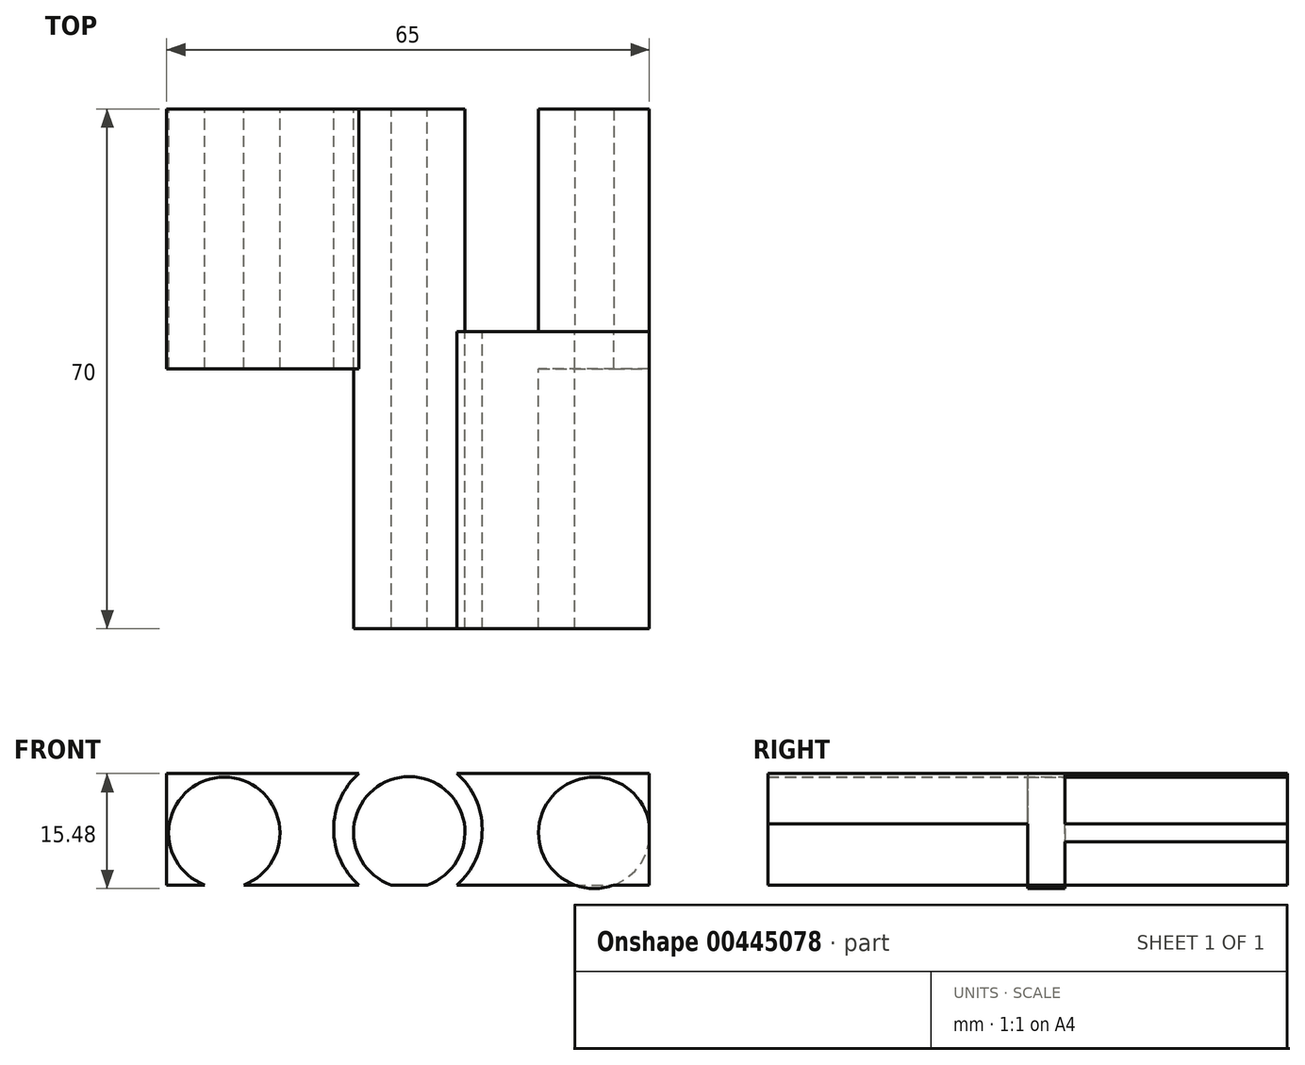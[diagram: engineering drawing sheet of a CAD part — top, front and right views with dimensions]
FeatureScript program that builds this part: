
annotation { "Feature Type Name" : "Feature", "Feature Type Description" : "" }
export const myFeature = defineFeature(function(context is Context, id is Id, definition is map)
    precondition{}
    {
        {
            var Q0;
            Q0=qCreatedBy(makeId("Front.planeOp"),FACE);
            var sketch = newSketch(context, id + "F0", { "sketchPlane" : qUnion([Q0])});
            skLineSegment(sketch, "E0.bottom", {"start": v(-32.5, 7.5) * mm, "end": v(32.5, 7.5) * mm});
            skLineSegment(sketch, "E0.top", {"start": v(-32.5, -7.5) * mm, "end": v(32.5, -7.5) * mm});
            skLineSegment(sketch, "E0.left", {"start": v(-32.5, 7.5) * mm, "end": v(-32.5, -7.5) * mm});
            skLineSegment(sketch, "E0.right", {"start": v(32.5, 7.5) * mm, "end": v(32.5, -7.5) * mm});
            skPoint(sketch, "E0.middle", {"position": v(0, 0) * mm});
            skPoint(sketch, "E1", {"position": v(0.19, -0.4) * mm});
            skCircle(sketch, "E2", {"center": v(0.19, -0.4) * mm, "radius": 7.5 * mm});
            skCircle(sketch, "E3", {"center": v(-24.73, -0.48) * mm, "radius": 7.5 * mm});
            skPoint(sketch, "E3.second.point", {"position": v(-32.23, -0.48) * mm});
            skPoint(sketch, "E3.third.point", {"position": v(-26.42, 6.83) * mm});
            skPoint(sketch, "E4.MirrorP", {"position": v(26.8, 6.83) * mm});
            skCircle(sketch, "E5.MirrorC", {"center": v(25.1, -0.48) * mm, "radius": 7.5 * mm});
            skCircle(sketch, "E6", {"center": v(0, 0) * mm, "radius": 10 * mm});
            skSolve(sketch);
        }
        {
            var Q0;
            {var subQ0=sQuery(id+"F0.wireOp",EDGE,"E3");var subQ1=sQuery(id+"F0.wireOp",EDGE,"E0.top");var subQ2=makeQuery(id+"F0.imprint","INTERSECT",VERTEX,{"disambiguationData":[OD(0.0)],"derivedFrom":[subQ1,subQ0]});Q0=makeQuery(id+"F0.imprint","IMPRINT",FACE,{"disambiguationData":[TD([[makeQuery(id+"F0.imprint","IMPRINT",EDGE,{"disambiguationData":[TD([[subQ2,-1.0]])],"derivedFrom":subQ1}),-1.0]])]});}
            var Q1;
            {var subQ0=sQuery(id+"F0.wireOp",EDGE,"E5.MirrorC");var subQ1=sQuery(id+"F0.wireOp",EDGE,"E0.top");var subQ2=makeQuery(id+"F0.imprint","INTERSECT",VERTEX,{"disambiguationData":[OD(0.0)],"derivedFrom":[subQ1,subQ0]});Q1=makeQuery(id+"F0.imprint","IMPRINT",FACE,{"disambiguationData":[TD([[makeQuery(id+"F0.imprint","IMPRINT",EDGE,{"disambiguationData":[TD([[subQ2,-1.0]])],"derivedFrom":subQ1}),-1.0]])]});}
            var Q2;
            {var subQ0=sQuery(id+"F0.wireOp",EDGE,"E0.right");var subQ1=sQuery(id+"F0.wireOp",EDGE,"E0.top");var subQ2=makeQuery(id+"F0.imprint","INTERSECT",VERTEX,{"derivedFrom":[subQ1,subQ0]});Q2=makeQuery(id+"F0.imprint","IMPRINT",FACE,{"disambiguationData":[TD([[makeQuery(id+"F0.imprint","IMPRINT",EDGE,{"disambiguationData":[TD([[subQ2,1.0]])],"derivedFrom":subQ1}),1.0]])]});}
            var Q3;
            {var subQ0=sQuery(id+"F0.wireOp",EDGE,"E5.MirrorC");var subQ1=sQuery(id+"F0.wireOp",EDGE,"E0.right");var subQ2=makeQuery(id+"F0.imprint","INTERSECT",VERTEX,{"disambiguationData":[OD(0.0)],"derivedFrom":[subQ1,subQ0]});Q3=makeQuery(id+"F0.imprint","IMPRINT",FACE,{"disambiguationData":[TD([[makeQuery(id+"F0.imprint","IMPRINT",EDGE,{"disambiguationData":[TD([[subQ2,-1.0]])],"derivedFrom":subQ1}),1.0]])]});}
            var Q4;
            {var subQ3=sQuery(id+"F0.wireOp",EDGE,"E0.right");var subQ5=sQuery(id+"F0.wireOp",EDGE,"E0.bottom");var subQ6=makeQuery(id+"F0.imprint","INTERSECT",VERTEX,{"derivedFrom":[subQ5,subQ3]});Q4=makeQuery(id+"F0.imprint","IMPRINT",FACE,{"disambiguationData":[TD([[makeQuery(id+"F0.imprint","IMPRINT",EDGE,{"disambiguationData":[TD([[subQ6,1.0]])],"derivedFrom":subQ5}),-1.0]])]});}
            var Q5;
            {var subQ4=sQuery(id+"F0.wireOp",EDGE,"E6");var subQ7=sQuery(id+"F0.wireOp",EDGE,"E0.bottom");var subQ8=makeQuery(id+"F0.imprint","INTERSECT",VERTEX,{"disambiguationData":[OD(0.0)],"derivedFrom":[subQ7,subQ4]});Q5=makeQuery(id+"F0.imprint","IMPRINT",FACE,{"disambiguationData":[TD([[makeQuery(id+"F0.imprint","IMPRINT",EDGE,{"disambiguationData":[TD([[subQ8,-1.0]])],"derivedFrom":subQ7}),-1.0]])]});}
            var Q6;
            {var subQ0=sQuery(id+"F0.wireOp",EDGE,"E0.left");Q6=makeQuery(id+"F0.imprint","IMPRINT",FACE,{"disambiguationData":[TD([[makeQuery(id+"F0.imprint","IMPRINT",EDGE,{"derivedFrom":subQ0}),1.0]])]});}
            var Q7;
            {var subQ0=sQuery(id+"F0.wireOp",EDGE,"E2");var subQ1=sQuery(id+"F0.wireOp",EDGE,"E0.top");var subQ2=makeQuery(id+"F0.imprint","INTERSECT",VERTEX,{"disambiguationData":[OD(0.0)],"derivedFrom":[subQ1,subQ0]});Q7=makeQuery(id+"F0.imprint","IMPRINT",FACE,{"disambiguationData":[TD([[makeQuery(id+"F0.imprint","IMPRINT",EDGE,{"disambiguationData":[TD([[subQ2,-1.0]])],"derivedFrom":subQ1}),1.0]])]});}
            var Q8;
            {var subQ0=sQuery(id+"F0.wireOp",EDGE,"E3");var subQ1=sQuery(id+"F0.wireOp",EDGE,"E0.top");var subQ2=makeQuery(id+"F0.imprint","INTERSECT",VERTEX,{"disambiguationData":[OD(0.0)],"derivedFrom":[subQ1,subQ0]});Q8=makeQuery(id+"F0.imprint","IMPRINT",FACE,{"disambiguationData":[TD([[makeQuery(id+"F0.imprint","IMPRINT",EDGE,{"disambiguationData":[TD([[subQ2,-1.0]])],"derivedFrom":subQ1}),1.0]])]});}
            var Q9;
            {var subQ0=sQuery(id+"F0.wireOp",EDGE,"E5.MirrorC");var subQ1=sQuery(id+"F0.wireOp",EDGE,"E0.top");var subQ2=makeQuery(id+"F0.imprint","INTERSECT",VERTEX,{"disambiguationData":[OD(0.0)],"derivedFrom":[subQ1,subQ0]});Q9=makeQuery(id+"F0.imprint","IMPRINT",FACE,{"disambiguationData":[TD([[makeQuery(id+"F0.imprint","IMPRINT",EDGE,{"disambiguationData":[TD([[subQ2,-1.0]])],"derivedFrom":subQ1}),1.0]])]});}
            extrude(context, id + "F1", {"entities" : qUnion([Q0, Q1, Q2, Q3, Q4, Q5, Q6, Q7, Q8, Q9]), "depth" : 5 * mm});
        }
        {
            var Q0;
            {var subQ0=sQuery(id+"F0.wireOp",EDGE,"E2");var subQ1=sQuery(id+"F0.wireOp",EDGE,"E0.top");var subQ2=makeQuery(id+"F0.imprint","INTERSECT",VERTEX,{"disambiguationData":[OD(0.0)],"derivedFrom":[subQ1,subQ0]});Q0=makeQuery(id+"F0.imprint","IMPRINT",FACE,{"disambiguationData":[TD([[makeQuery(id+"F0.imprint","IMPRINT",EDGE,{"disambiguationData":[TD([[subQ2,-1.0]])],"derivedFrom":subQ1}),1.0]])]});}
            var Q1;
            {var subQ0=sQuery(id+"F0.wireOp",EDGE,"E6");var subQ1=sQuery(id+"F0.wireOp",EDGE,"E0.bottom");var subQ2=makeQuery(id+"F0.imprint","INTERSECT",VERTEX,{"disambiguationData":[OD(0.0)],"derivedFrom":[subQ1,subQ0]});Q1=makeQuery(id+"F0.imprint","IMPRINT",FACE,{"disambiguationData":[TD([[makeQuery(id+"F0.imprint","IMPRINT",EDGE,{"disambiguationData":[TD([[subQ2,-1.0]])],"derivedFrom":subQ1}),1.0]])]});}
            var Q2;
            {var subQ0=sQuery(id+"F0.wireOp",EDGE,"E6");var subQ1=sQuery(id+"F0.wireOp",EDGE,"E0.top");var subQ2=makeQuery(id+"F0.imprint","INTERSECT",VERTEX,{"disambiguationData":[OD(0.0)],"derivedFrom":[subQ1,subQ0]});Q2=makeQuery(id+"F0.imprint","IMPRINT",FACE,{"disambiguationData":[TD([[makeQuery(id+"F0.imprint","IMPRINT",EDGE,{"disambiguationData":[TD([[subQ2,-1.0]])],"derivedFrom":subQ1}),-1.0]])]});}
            var Q3;
            {var subQ4=sQuery(id+"F0.wireOp",EDGE,"E6");var subQ7=sQuery(id+"F0.wireOp",EDGE,"E0.bottom");var subQ8=makeQuery(id+"F0.imprint","INTERSECT",VERTEX,{"disambiguationData":[OD(0.0)],"derivedFrom":[subQ7,subQ4]});Q3=makeQuery(id+"F0.imprint","IMPRINT",FACE,{"disambiguationData":[TD([[makeQuery(id+"F0.imprint","IMPRINT",EDGE,{"disambiguationData":[TD([[subQ8,-1.0]])],"derivedFrom":subQ7}),-1.0]])]});}
            extrude(context, id + "F2", {"entities" : qUnion([Q0, Q1, Q2, Q3]), "operationType" : NewBodyOperationType.ADD, "depth" : 40 * mm});
        }
        {
            var Q0;
            {var subQ0=sQuery(id+"F0.wireOp",EDGE,"E5.MirrorC");var subQ1=sQuery(id+"F0.wireOp",EDGE,"E0.top");var subQ2=makeQuery(id+"F0.imprint","INTERSECT",VERTEX,{"disambiguationData":[OD(0.0)],"derivedFrom":[subQ1,subQ0]});Q0=makeQuery(id+"F0.imprint","IMPRINT",FACE,{"disambiguationData":[TD([[makeQuery(id+"F0.imprint","IMPRINT",EDGE,{"disambiguationData":[TD([[subQ2,-1.0]])],"derivedFrom":subQ1}),1.0]])]});}
            var Q1;
            {var subQ0=sQuery(id+"F0.wireOp",EDGE,"E3");var subQ1=sQuery(id+"F0.wireOp",EDGE,"E0.top");var subQ2=makeQuery(id+"F0.imprint","INTERSECT",VERTEX,{"disambiguationData":[OD(0.0)],"derivedFrom":[subQ1,subQ0]});Q1=makeQuery(id+"F0.imprint","IMPRINT",FACE,{"disambiguationData":[TD([[makeQuery(id+"F0.imprint","IMPRINT",EDGE,{"disambiguationData":[TD([[subQ2,-1.0]])],"derivedFrom":subQ1}),1.0]])]});}
            var Q2;
            {var subQ0=sQuery(id+"F0.wireOp",EDGE,"E2");var subQ1=sQuery(id+"F0.wireOp",EDGE,"E0.top");var subQ2=makeQuery(id+"F0.imprint","INTERSECT",VERTEX,{"disambiguationData":[OD(0.0)],"derivedFrom":[subQ1,subQ0]});Q2=makeQuery(id+"F0.imprint","IMPRINT",FACE,{"disambiguationData":[TD([[makeQuery(id+"F0.imprint","IMPRINT",EDGE,{"disambiguationData":[TD([[subQ2,-1.0]])],"derivedFrom":subQ1}),1.0]])]});}
            extrude(context, id + "F3", {"entities" : qUnion([Q0, Q1, Q2]), "operationType" : NewBodyOperationType.ADD, "oppositeDirection" : true, "depth" : 30 * mm});
        }
    });
